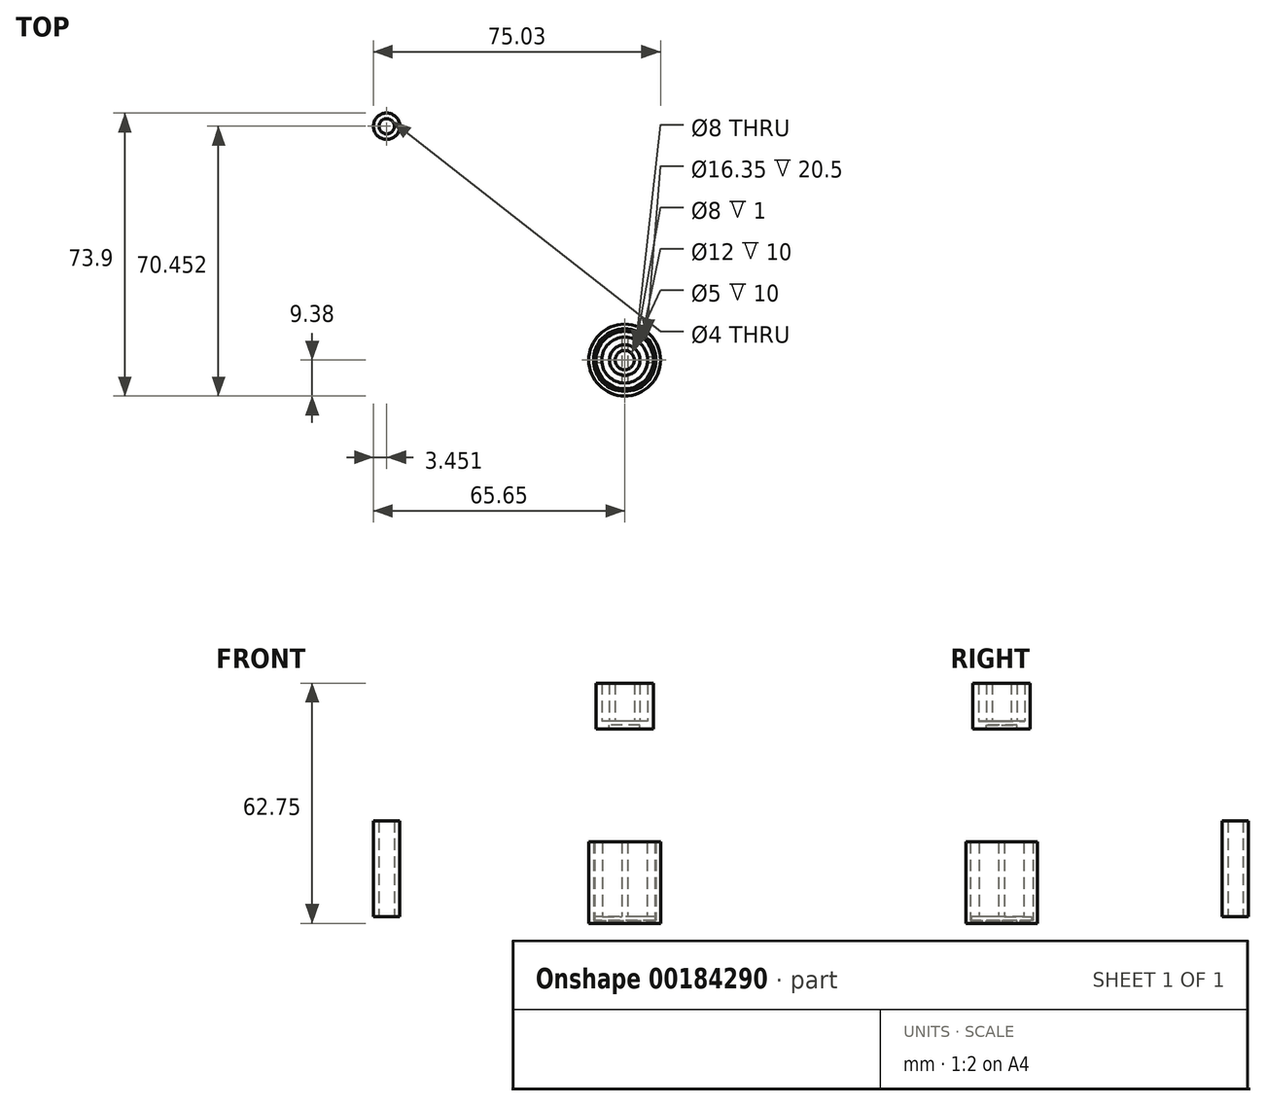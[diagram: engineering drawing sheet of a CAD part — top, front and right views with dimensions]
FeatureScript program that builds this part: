
annotation { "Feature Type Name" : "Feature", "Feature Type Description" : "" }
export const myFeature = defineFeature(function(context is Context, id is Id, definition is map)
    precondition{}
    {
        {
            assignVariable(context, id + "F0", {"name" : "wellHeight", "anyValue" : 19.5});
        }
        {
            var Q0;
            Q0=qCreatedBy(makeId("Top.planeOp"),FACE);
            var sketch = newSketch(context, id + "F1", { "sketchPlane" : qUnion([Q0])});
            skCircle(sketch, "E0", {"center": v(0, 0) * mm, "radius": 7.88 * mm});
            skArc(sketch, "E1", {"start": v(-7.84, -0.75) * mm, "mid": v(0, -7.88) * mm, "end": v(7.84, -0.75) * mm});
            skArc(sketch, "E2", {"start": v(-0.75, 5.83) * mm, "mid": v(-4.15, 4.15) * mm, "end": v(-5.83, 0.75) * mm});
            skLineSegment(sketch, "E3", {"start": v(-0.75, 5.83) * mm, "end": v(-0.75, -5.83) * mm});
            skLineSegment(sketch, "E4", {"start": v(0.75, 5.83) * mm, "end": v(0.75, -5.83) * mm});
            skLineSegment(sketch, "E5", {"start": v(7.84, 0.75) * mm, "end": v(5.83, 0.75) * mm});
            skLineSegment(sketch, "E6", {"start": v(7.84, -0.75) * mm, "end": v(5.83, -0.75) * mm});
            skLineSegment(sketch, "E7", {"start": v(0, 14.94) * mm, "end": v(0, -13.82) * mm, "construction": true});
            skPoint(sketch, "E7.endSnap0", {"position": v(0, -0.75) * mm});
            skLineSegment(sketch, "E8", {"start": v(17.32, 0) * mm, "end": v(-18.56, 0) * mm, "construction": true});
            skArc(sketch, "E9.trimOffspring", {"start": v(-5.83, -0.75) * mm, "mid": v(-4.15, -4.15) * mm, "end": v(-0.75, -5.83) * mm});
            skLineSegment(sketch, "E10.trimOffspring", {"start": v(-5.83, 0.75) * mm, "end": v(-7.84, 0.75) * mm});
            skLineSegment(sketch, "E11.trimOffspring", {"start": v(-5.83, -0.75) * mm, "end": v(-7.84, -0.75) * mm});
            skArc(sketch, "E12.trimOffspring", {"start": v(5.83, 0.75) * mm, "mid": v(4.15, 4.15) * mm, "end": v(0.75, 5.83) * mm});
            skArc(sketch, "E13.trimOffspring", {"start": v(7.84, 0.75) * mm, "mid": v(0, 7.87) * mm, "end": v(-7.84, 0.75) * mm});
            skArc(sketch, "E14.trimOffspring", {"start": v(0.75, -5.83) * mm, "mid": v(4.15, -4.15) * mm, "end": v(5.83, -0.75) * mm});
            skSolve(sketch);
        }
        {
            var Q0;
            Q0=makeQuery(id+"F1.imprint","IMPRINT",FACE,{"disambiguationData":[TD([[makeQuery(id+"F1.imprint","IMPRINT",EDGE,{"derivedFrom":sQuery(id+"F1.wireOp",EDGE,"E2")}),1.0]])]});
            var Q1;
            Q1=makeQuery(id+"F1.imprint","IMPRINT",FACE,{"disambiguationData":[TD([[makeQuery(id+"F1.imprint","IMPRINT",EDGE,{"derivedFrom":sQuery(id+"F1.wireOp",EDGE,"E4")}),1.0]])]});
            extrude(context, id + "F2", {"entities" : qUnion([Q0, Q1]), "depth" : (getVariable(context, 'wellHeight')) * mm});
        }
        {
            var Q0;
            Q0=makeQuery(id+"F1.imprint","IMPRINT",FACE,{"disambiguationData":[TD([[makeQuery(id+"F1.imprint","IMPRINT",EDGE,{"derivedFrom":sQuery(id+"F1.wireOp",EDGE,"E2")}),-1.0]])]});
            var Q1;
            Q1=makeQuery(id+"F1.imprint","IMPRINT",FACE,{"disambiguationData":[TD([[makeQuery(id+"F1.imprint","IMPRINT",EDGE,{"derivedFrom":sQuery(id+"F1.wireOp",EDGE,"E2")}),1.0]])]});
            var Q2;
            Q2=makeQuery(id+"F1.imprint","IMPRINT",FACE,{"disambiguationData":[TD([[makeQuery(id+"F1.imprint","IMPRINT",EDGE,{"derivedFrom":sQuery(id+"F1.wireOp",EDGE,"E4")}),1.0]])]});
            extrude(context, id + "F3", {"entities" : qUnion([Q0, Q1, Q2]), "operationType" : NewBodyOperationType.ADD, "oppositeDirection" : true, "depth" : 1 * mm});
        }
        {
            var Q0;
            Q0=makeQuery(id+"F3.opExtrude","CAP_FACE",FACE,{"disambiguationData":[OSD([sQuery(id+"F1.wireOp",EDGE,"E0")])],"isStart":false});
            var sketch = newSketch(context, id + "F4", { "sketchPlane" : qUnion([Q0])});
            skCircle(sketch, "E15", {"center": v(0, 0) * mm, "radius": 9.38 * mm});
            skCircle(sketch, "E16", {"center": v(0, 0) * mm, "radius": 8.18 * mm});
            skCircle(sketch, "E17", {"center": v(0, 0) * mm, "radius": 4 * mm});
            skSolve(sketch);
        }
        {
            var Q0;
            Q0=makeQuery(id+"F4.imprint","IMPRINT",FACE,{"disambiguationData":[TD([[makeQuery(id+"F4.imprint","IMPRINT",EDGE,{"derivedFrom":sQuery(id+"F4.wireOp",EDGE,"E15")}),1.0]])]});
            var Q1;
            Q1=makeQuery(id+"F4.imprint","IMPRINT",FACE,{"disambiguationData":[TD([[makeQuery(id+"F4.imprint","IMPRINT",EDGE,{"derivedFrom":sQuery(id+"F4.wireOp",EDGE,"E16")}),1.0]])]});
            var Q2;
            Q2=makeQuery(id+"F4.imprint","IMPRINT",FACE,{"disambiguationData":[TD([[makeQuery(id+"F4.imprint","IMPRINT",EDGE,{"derivedFrom":makeQuery(id+"F3.opExtrude","CAP_EDGE",EDGE,{"disambiguationData":[OSD([sQuery(id+"F1.wireOp",EDGE,"E0")])],"isStart":false})}),-1.0]])]});
            extrude(context, id + "F5", {"entities" : qUnion([Q0, Q1, Q2]), "depth" : .75 * mm});
        }
        {
            var Q0;
            Q0=makeQuery(id+"F4.imprint","IMPRINT",FACE,{"disambiguationData":[TD([[makeQuery(id+"F4.imprint","IMPRINT",EDGE,{"derivedFrom":sQuery(id+"F4.wireOp",EDGE,"E15")}),1.0]])]});
            extrude(context, id + "F6", {"entities" : qUnion([Q0]), "operationType" : NewBodyOperationType.ADD, "oppositeDirection" : true, "depth" : (getVariable(context, 'wellHeight') + 1) * mm});
        }
        {
            var Q0;
            Q0=qCreatedBy(makeId("Top.planeOp"),FACE);
            cPlane(context, id + "F7", {"entities" : qUnion([Q0]), "cplaneType" : CPlaneType.OFFSET, "offset" : 50 * mm, "width" : 150 * mm, "height" : 150 * mm});
        }
        {
            var Q0;
            Q0=qCreatedBy(id+"F7.planeOp",FACE);
            var sketch = newSketch(context, id + "F8", { "sketchPlane" : qUnion([Q0])});
            skCircle(sketch, "E18", {"center": v(0, 0) * mm, "radius": 7.5 * mm});
            skCircle(sketch, "E19", {"center": v(0, 0) * mm, "radius": 6 * mm});
            skCircle(sketch, "E20", {"center": v(0, 0) * mm, "radius": 4 * mm});
            skSolve(sketch);
        }
        {
            var Q0;
            Q0=makeQuery(id+"F8.imprint","IMPRINT",FACE,{"disambiguationData":[TD([[makeQuery(id+"F8.imprint","IMPRINT",EDGE,{"derivedFrom":sQuery(id+"F8.wireOp",EDGE,"E18")}),1.0]])]});
            var Q1;
            Q1=makeQuery(id+"F8.imprint","IMPRINT",FACE,{"disambiguationData":[TD([[makeQuery(id+"F8.imprint","IMPRINT",EDGE,{"derivedFrom":sQuery(id+"F8.wireOp",EDGE,"E19")}),1.0]])]});
            extrude(context, id + "F9", {"entities" : qUnion([Q0, Q1]), "oppositeDirection" : true, "depth" : 1 * mm});
        }
        {
            var Q0;
            Q0=makeQuery(id+"F8.imprint","IMPRINT",FACE,{"disambiguationData":[TD([[makeQuery(id+"F8.imprint","IMPRINT",EDGE,{"derivedFrom":sQuery(id+"F8.wireOp",EDGE,"E18")}),1.0]])]});
            extrude(context, id + "F10", {"entities" : qUnion([Q0]), "operationType" : NewBodyOperationType.ADD, "depth" : 11 * mm});
        }
        {
            var Q0;
            Q0=qCreatedBy(id+"F7.planeOp",FACE);
            var sketch = newSketch(context, id + "F11", { "sketchPlane" : qUnion([Q0])});
            skCircle(sketch, "E21", {"center": v(0, 0) * mm, "radius": 4 * mm});
            skCircle(sketch, "E22", {"center": v(0, 0) * mm, "radius": 2.5 * mm});
            skCircle(sketch, "E23", {"center": v(0, 0) * mm, "radius": 6 * mm});
            skSolve(sketch);
        }
        {
            var Q0;
            Q0=makeQuery(id+"F8.imprint","IMPRINT",FACE,{"disambiguationData":[TD([[makeQuery(id+"F8.imprint","IMPRINT",EDGE,{"derivedFrom":sQuery(id+"F8.wireOp",EDGE,"E19")}),1.0]])]});
            var Q1;
            Q1=makeQuery(id+"F8.imprint","IMPRINT",FACE,{"disambiguationData":[TD([[makeQuery(id+"F8.imprint","IMPRINT",EDGE,{"derivedFrom":sQuery(id+"F8.wireOp",EDGE,"E20")}),1.0]])]});
            extrude(context, id + "F12", {"entities" : qUnion([Q0, Q1]), "depth" : 1 * mm});
        }
        {
            var Q0;
            Q0=makeQuery(id+"F11.imprint","IMPRINT",FACE,{"disambiguationData":[TD([[makeQuery(id+"F11.imprint","IMPRINT",EDGE,{"derivedFrom":sQuery(id+"F11.wireOp",EDGE,"E21")}),1.0]])]});
            extrude(context, id + "F13", {"entities" : qUnion([Q0]), "operationType" : NewBodyOperationType.ADD, "depth" : 11 * mm});
        }
        {
            var Q0;
            Q0=qCreatedBy(makeId("Top.planeOp"),FACE);
            var sketch = newSketch(context, id + "F14", { "sketchPlane" : qUnion([Q0])});
            skCircle(sketch, "E24", {"center": v(-62.2, 61.07) * mm, "radius": 3.45 * mm});
            skCircle(sketch, "E25", {"center": v(-62.2, 61.07) * mm, "radius": 2 * mm});
            skSolve(sketch);
        }
        {
            var Q0;
            Q0=makeQuery(id+"F14.imprint","IMPRINT",FACE,{"disambiguationData":[TD([[makeQuery(id+"F14.imprint","IMPRINT",EDGE,{"derivedFrom":sQuery(id+"F14.wireOp",EDGE,"E24")}),1.0]])]});
            extrude(context, id + "F15", {"entities" : qUnion([Q0]), "depth" : 25 * mm});
        }
    });
